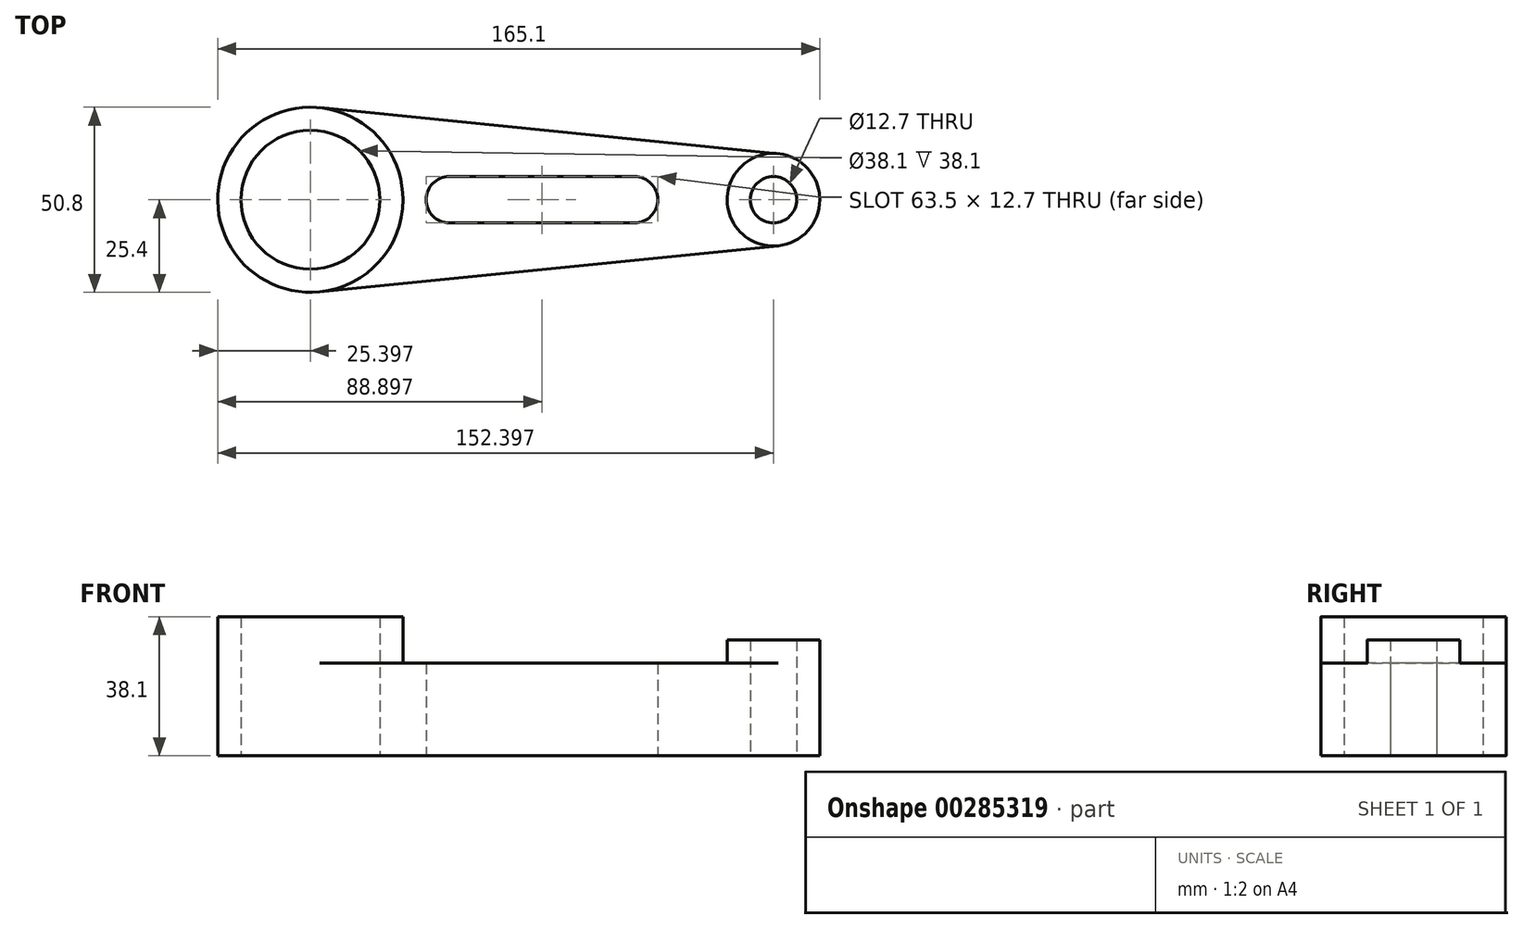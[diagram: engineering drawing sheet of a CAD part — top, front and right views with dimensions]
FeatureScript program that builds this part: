
annotation { "Feature Type Name" : "Feature", "Feature Type Description" : "" }
export const myFeature = defineFeature(function(context is Context, id is Id, definition is map)
    precondition{}
    {
        {
            var Q0;
            Q0=qCreatedBy(makeId("Top.planeOp"),FACE);
            var sketch = newSketch(context, id + "F0", { "sketchPlane" : qUnion([Q0])});
            skCircle(sketch, "E0", {"center": v(-44, 6.35) * mm, "radius": 25.4 * mm});
            skCircle(sketch, "E1", {"center": v(-44, 6.35) * mm, "radius": 19.05 * mm});
            skCircle(sketch, "E2", {"center": v(83, 6.35) * mm, "radius": 12.7 * mm});
            skCircle(sketch, "E3", {"center": v(83, 6.35) * mm, "radius": 6.35 * mm});
            skLineSegment(sketch, "E4", {"start": v(-41.45, 31.62) * mm, "end": v(84.28, 18.99) * mm});
            skLineSegment(sketch, "E5", {"start": v(-41.45, -18.92) * mm, "end": v(84.28, -6.29) * mm});
            skCircle(sketch, "E6", {"center": v(-5.9, 6.35) * mm, "radius": 6.35 * mm});
            skCircle(sketch, "E7", {"center": v(44.9, 6.35) * mm, "radius": 6.35 * mm});
            skLineSegment(sketch, "E8", {"start": v(-5.9, 12.7) * mm, "end": v(44.9, 12.7) * mm});
            skLineSegment(sketch, "E9", {"start": v(-5.9, 0) * mm, "end": v(44.9, 0) * mm});
            skPoint(sketch, "E10.orphan", {"position": v(0, 12.7) * mm});
            skPoint(sketch, "E11.orphan", {"position": v(44.9, 0) * mm});
            skSolve(sketch);
        }
        {
            var Q0;
            Q0 = qSketchRegion(id + "F0", true);
            extrude(context, id + "F1", {"entities" : qUnion([Q0]), "depth" : 25.4 * mm});
        }
        {
            var Q0;
            Q0=makeQuery(id+"F1.opExtrude","CAP_FACE",FACE,{"disambiguationData":[OSD([sQuery(id+"F0.wireOp",EDGE,"E0"),sQuery(id+"F0.wireOp",EDGE,"E1"),sQuery(id+"F0.wireOp",EDGE,"E2"),sQuery(id+"F0.wireOp",EDGE,"E3"),sQuery(id+"F0.wireOp",EDGE,"E4"),sQuery(id+"F0.wireOp",EDGE,"E5"),sQuery(id+"F0.wireOp",EDGE,"E6"),sQuery(id+"F0.wireOp",EDGE,"E7"),sQuery(id+"F0.wireOp",EDGE,"E8"),sQuery(id+"F0.wireOp",EDGE,"E9")])],"isStart":false});
            var sketch = newSketch(context, id + "F2", { "sketchPlane" : qUnion([Q0])});
            skCircle(sketch, "E12", {"center": v(-44, 6.35) * mm, "radius": 25.4 * mm});
            skCircle(sketch, "E13", {"center": v(-44, 6.35) * mm, "radius": 19.05 * mm});
            skSolve(sketch);
        }
        {
            var Q0;
            Q0 = qSketchRegion(id + "F2", true);
            extrude(context, id + "F3", {"entities" : qUnion([Q0]), "operationType" : NewBodyOperationType.ADD, "depth" : 12.7 * mm});
        }
        {
            var Q0;
            Q0=makeQuery(id+"F1.opExtrude","CAP_FACE",FACE,{"disambiguationData":[OSD([sQuery(id+"F0.wireOp",EDGE,"E0"),sQuery(id+"F0.wireOp",EDGE,"E1"),sQuery(id+"F0.wireOp",EDGE,"E2"),sQuery(id+"F0.wireOp",EDGE,"E3"),sQuery(id+"F0.wireOp",EDGE,"E4"),sQuery(id+"F0.wireOp",EDGE,"E5"),sQuery(id+"F0.wireOp",EDGE,"E6"),sQuery(id+"F0.wireOp",EDGE,"E7"),sQuery(id+"F0.wireOp",EDGE,"E8"),sQuery(id+"F0.wireOp",EDGE,"E9")])],"isStart":false});
            var sketch = newSketch(context, id + "F4", { "sketchPlane" : qUnion([Q0])});
            skCircle(sketch, "E14", {"center": v(83, 6.35) * mm, "radius": 12.7 * mm});
            skCircle(sketch, "E15", {"center": v(83, 6.35) * mm, "radius": 6.35 * mm});
            skSolve(sketch);
        }
        {
            var Q0;
            Q0 = qSketchRegion(id + "F4", true);
            extrude(context, id + "F5", {"entities" : qUnion([Q0]), "operationType" : NewBodyOperationType.ADD, "depth" : 6.35 * mm});
        }
    });
